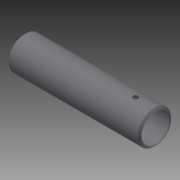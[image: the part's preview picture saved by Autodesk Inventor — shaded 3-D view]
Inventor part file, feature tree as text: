
AUTODESK INVENTOR PART (.ipt)
format: ipt  version: 2014 (Build 180170000, 170)  size: 134,144 bytes
history: native  units: in
note: dims shown in document units (in); Inventor stores cm internally (conversion verified against a paired STEP export)
features: other x56, revolve x2, sketch x2
ambient origin geometry x8: Origin, YZ Plane, XZ Plane, XY Plane, X Axis, Y Axis, Z Axis, Center Point
bodies: Solid1 (feature_tree)
feature tree (60):
  revolve  "Revolution1"  Angle=360.0deg
  revolve  "Revolution2"  [1 undecoded]
  other  "o1_XY"
  other  "o1_YZ"
  other  "o1_ZX"
  other  "o1_X"
  other  "o1_Y"
  other  "o1_Z"
  other  "o1_Center"
  other  "o2_XY"
  other  "o2_YZ"
  other  "o2_ZX"
  other  "o2_X"
  other  "o2_Y"
  other  "o2_Z"
  other  "o2_Center"
  other  "t1_XY"
  other  "t1_YZ"
  other  "t1_ZX"
  other  "t1_X"
  other  "t1_Y"
  other  "t1_Z"
  other  "t1_Center"
  other  "t2_XY"
  other  "t2_YZ"
  other  "t2_ZX"
  other  "t2_X"
  other  "t2_Y"
  other  "t2_Z"
  other  "t2_Center"
  other  "t3_XY"
  other  "t3_YZ"
  other  "t3_ZX"
  other  "t3_X"
  other  "t3_Y"
  other  "t3_Z"
  other  "t3_Center"
  other  "t4_XY"
  other  "t4_YZ"
  other  "t4_ZX"
  other  "t4_X"
  other  "t4_Y"
  other  "t4_Z"
  other  "t4_Center"
  other  "tube1_XY"
  other  "tube1_YZ"
  other  "tube1_ZX"
  other  "tube1_X"
  other  "tube1_Y"
  other  "tube1_Z"
  other  "tube1_Center"
  other  "tube2_XY"
  other  "tube2_YZ"
  other  "tube2_ZX"
  other  "tube2_X"
  other  "tube2_Y"
  other  "tube2_Z"
  other  "tube2_Center"
  sketch  "Sketch_5"
  sketch  "Sketch_1"  dims[d0=360.0deg d1=360.0deg]
note: 1 required parameter value undecoded (feature->parameter linkage not recoverable at this tier; creation-order binding heuristic only, values carry confidence <= 0.55)
